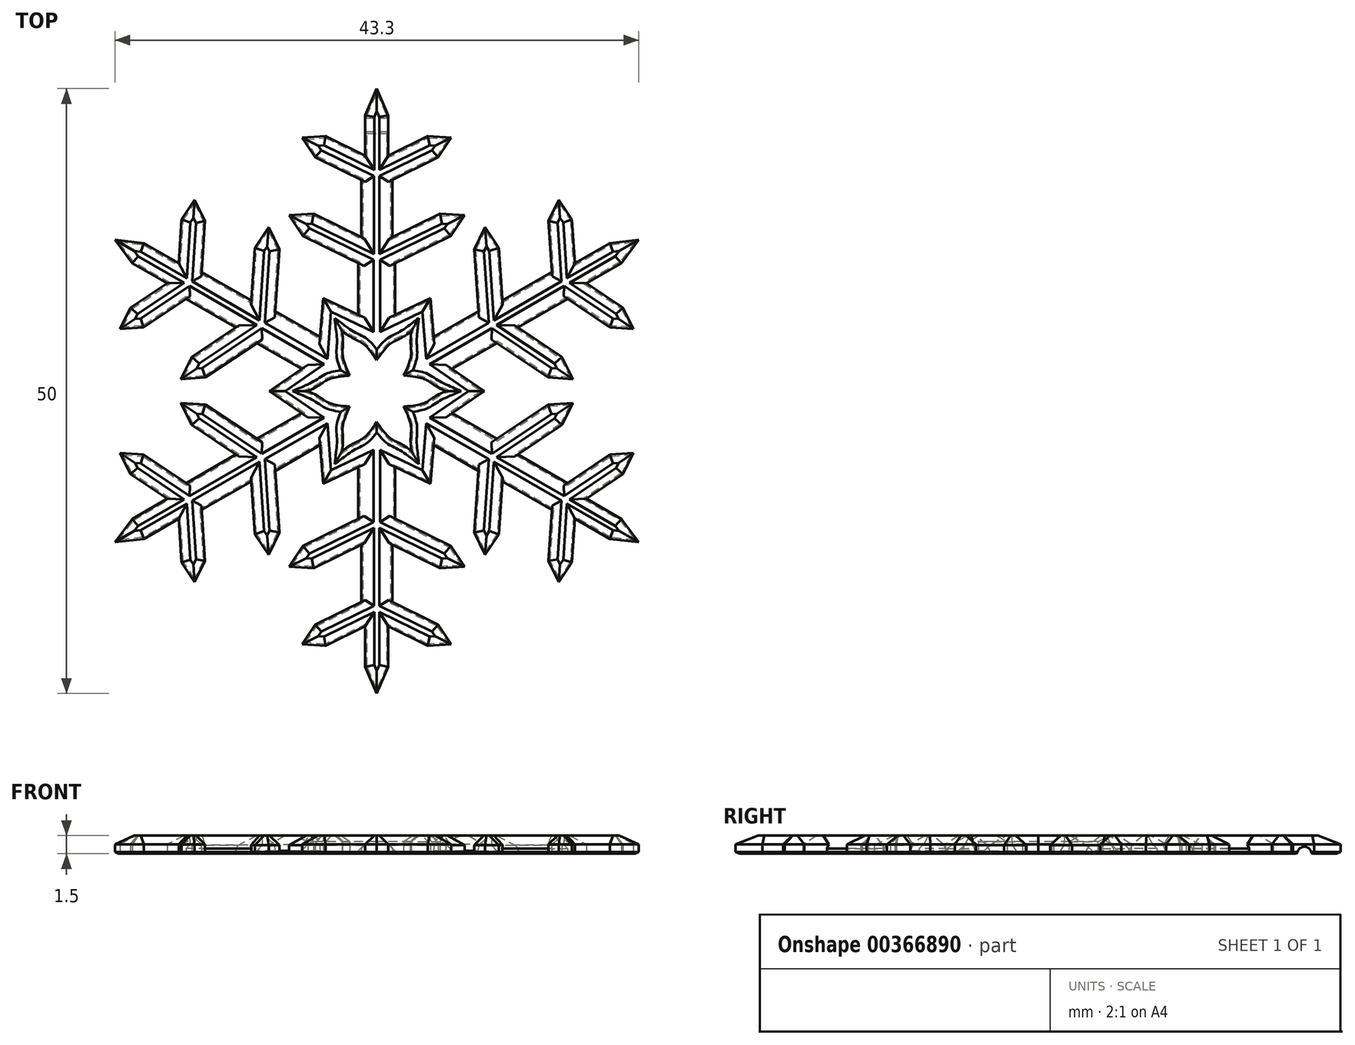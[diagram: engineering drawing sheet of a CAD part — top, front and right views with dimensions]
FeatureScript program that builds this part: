
annotation { "Feature Type Name" : "Feature", "Feature Type Description" : "" }
export const myFeature = defineFeature(function(context is Context, id is Id, definition is map)
    precondition{}
    {
        {
            var Q0;
            Q0=qCreatedBy(makeId("Top.planeOp"),FACE);
            var sketch = newSketch(context, id + "F0", { "sketchPlane" : qUnion([Q0])});
            skLineSegment(sketch, "E0", {"start": v(0, 0) * mm, "end": v(0, 29.9) * mm, "construction": true});
            skCircle(sketch, "E1", {"center": v(0, 0) * mm, "radius": 25 * mm, "construction": true});
            skLineSegment(sketch, "E2", {"start": v(0, 25) * mm, "end": v(0.95, 22.8) * mm});
            skLineSegment(sketch, "E3", {"start": v(0.95, 22.8) * mm, "end": v(0.95, 19.45) * mm});
            skLineSegment(sketch, "E4", {"start": v(0.95, 19.45) * mm, "end": v(4.22, 21.06) * mm});
            skLineSegment(sketch, "E5", {"start": v(4.22, 21.06) * mm, "end": v(6.16, 20.93) * mm});
            skLineSegment(sketch, "E6", {"start": v(6.16, 20.93) * mm, "end": v(5.08, 19.32) * mm});
            skLineSegment(sketch, "E7", {"start": v(5.08, 19.32) * mm, "end": v(1.28, 17.45) * mm});
            skLineSegment(sketch, "E8", {"start": v(1.28, 17.45) * mm, "end": v(1.28, 12.72) * mm});
            skLineSegment(sketch, "E9", {"start": v(1.28, 12.72) * mm, "end": v(5.21, 14.66) * mm});
            skLineSegment(sketch, "E10", {"start": v(5.21, 14.66) * mm, "end": v(7.25, 14.52) * mm});
            skLineSegment(sketch, "E11", {"start": v(7.25, 14.52) * mm, "end": v(6.11, 12.82) * mm});
            skLineSegment(sketch, "E12", {"start": v(6.11, 12.82) * mm, "end": v(1.52, 10.57) * mm});
            skLineSegment(sketch, "E13", {"start": v(1.52, 10.57) * mm, "end": v(1.52, 6.3) * mm});
            skLineSegment(sketch, "E14", {"start": v(1.52, 6.3) * mm, "end": v(4.43, 7.68) * mm});
            skLineSegment(sketch, "E15.MirrorCS", {"start": v(-0.95, 22.8) * mm, "end": v(-0.95, 19.45) * mm});
            skLineSegment(sketch, "E16.MirrorCS", {"start": v(-4.22, 21.06) * mm, "end": v(-6.16, 20.93) * mm});
            skLineSegment(sketch, "E17.MirrorCS", {"start": v(-0.95, 19.45) * mm, "end": v(-4.22, 21.06) * mm});
            skLineSegment(sketch, "E18.MirrorCS", {"start": v(-1.28, 12.72) * mm, "end": v(-5.21, 14.66) * mm});
            skLineSegment(sketch, "E19.MirrorCS", {"start": v(-5.21, 14.66) * mm, "end": v(-7.25, 14.52) * mm});
            skLineSegment(sketch, "E20.MirrorCS", {"start": v(-7.25, 14.52) * mm, "end": v(-6.11, 12.82) * mm});
            skLineSegment(sketch, "E21.MirrorCS", {"start": v(-1.28, 17.45) * mm, "end": v(-1.28, 12.72) * mm});
            skLineSegment(sketch, "E22.MirrorCS", {"start": v(0, 25) * mm, "end": v(-0.95, 22.8) * mm});
            skLineSegment(sketch, "E23.MirrorCS", {"start": v(-6.16, 20.93) * mm, "end": v(-5.08, 19.32) * mm});
            skLineSegment(sketch, "E24.MirrorCS", {"start": v(-5.08, 19.32) * mm, "end": v(-1.28, 17.45) * mm});
            skLineSegment(sketch, "E25.MirrorCS", {"start": v(-6.11, 12.82) * mm, "end": v(-1.52, 10.57) * mm});
            skLineSegment(sketch, "E26", {"start": v(0, 0) * mm, "end": v(0, 30.32) * mm, "construction": true});
            skLineSegment(sketch, "E27", {"start": v(0, 0) * mm, "end": v(17.52, 30.35) * mm, "construction": true});
            skLineSegment(sketch, "E28", {"start": v(0, 0) * mm, "end": v(-18.63, 32.26) * mm, "construction": true});
            skLineSegment(sketch, "E29", {"start": v(4.43, 7.68) * mm, "end": v(2.85, 4.93) * mm});
            skLineSegment(sketch, "E30.MirrorCS", {"start": v(-1.52, 10.57) * mm, "end": v(-1.52, 6.3) * mm});
            skLineSegment(sketch, "E31.MirrorCS", {"start": v(-1.52, 6.3) * mm, "end": v(-4.43, 7.68) * mm});
            skFitSpline(sketch, "E32", {"points": [v(2.85, 4.93) * mm, v(0, 2.57) * mm], "startDerivative": vector(-4.57, -3.43) * mm, "endDerivative": vector(-3.94, -5.85) * mm});
            skFitSpline(sketch, "E33.MirrorCS", {"points": [v(-2.85, 4.93) * mm, v(0, 2.57) * mm], "startDerivative": vector(4.57, -3.43) * mm, "endDerivative": vector(3.94, -5.85) * mm});
            skLineSegment(sketch, "E34.MirrorCS", {"start": v(-4.43, 7.68) * mm, "end": v(-2.85, 4.93) * mm});
            skSolve(sketch);
        }
        {
            var Q0;
            Q0=makeQuery(id+"F0.imprint","IMPRINT",FACE,{"disambiguationData":[TD([[makeQuery(id+"F0.imprint","IMPRINT",EDGE,{"derivedFrom":sQuery(id+"F0.wireOp",EDGE,"E2")}),-1.0]])]});
            extrude(context, id + "F1", {"entities" : qUnion([Q0]), "endBound" : BoundingType.SYMMETRIC, "depth" : 1.5 * mm});
        }
        {
            var Q0;
            Q0=qCreatedBy(makeId("Front.planeOp"),FACE);
            var sketch = newSketch(context, id + "F2", { "sketchPlane" : qUnion([Q0])});
            skLineSegment(sketch, "E35", {"start": v(0, -15.67) * mm, "end": v(0, 28.6) * mm, "construction": true});
            skSolve(sketch);
        }
        {
            var Q0;
            Q0=makeQuery(id+"F1.opExtrude","SWEPT_BODY",BODY,{"disambiguationData":[OSD([sQuery(id+"F0.wireOp",EDGE,"E2"),sQuery(id+"F0.wireOp",EDGE,"E3"),sQuery(id+"F0.wireOp",EDGE,"E4"),sQuery(id+"F0.wireOp",EDGE,"E5"),sQuery(id+"F0.wireOp",EDGE,"E6"),sQuery(id+"F0.wireOp",EDGE,"E7"),sQuery(id+"F0.wireOp",EDGE,"E8"),sQuery(id+"F0.wireOp",EDGE,"E9"),sQuery(id+"F0.wireOp",EDGE,"E10"),sQuery(id+"F0.wireOp",EDGE,"E11"),sQuery(id+"F0.wireOp",EDGE,"E12"),sQuery(id+"F0.wireOp",EDGE,"E13"),sQuery(id+"F0.wireOp",EDGE,"E14"),sQuery(id+"F0.wireOp",EDGE,"b2b48e4d-2c92-4a1f-81ad-3469f6dd68cb"),sQuery(id+"F0.wireOp",EDGE,"E15.MirrorCS"),sQuery(id+"F0.wireOp",EDGE,"E16.MirrorCS"),sQuery(id+"F0.wireOp",EDGE,"E17.MirrorCS"),sQuery(id+"F0.wireOp",EDGE,"E18.MirrorCS"),sQuery(id+"F0.wireOp",EDGE,"E19.MirrorCS"),sQuery(id+"F0.wireOp",EDGE,"E20.MirrorCS"),sQuery(id+"F0.wireOp",EDGE,"E21.MirrorCS"),sQuery(id+"F0.wireOp",EDGE,"E22.MirrorCS"),sQuery(id+"F0.wireOp",EDGE,"E23.MirrorCS"),sQuery(id+"F0.wireOp",EDGE,"E24.MirrorCS"),sQuery(id+"F0.wireOp",EDGE,"E160.MirrorCS"),sQuery(id+"F0.wireOp",EDGE,"E25.MirrorCS"),sQuery(id+"F0.wireOp",EDGE,"4b62aa35-2862-45d5-86f5-f30a92808e40"),sQuery(id+"F0.wireOp",EDGE,"c1be86ca-d8b8-4c1e-b1f3-8d63ae980cd1")])]});
            var Q1;
            Q1=sQuery(id+"F2.wireOp",EDGE,"E35");
            circularPattern(context, id + "F3", {"operationType" : NewBodyOperationType.ADD, "entities" : qUnion([Q0]), "axis" : qUnion([Q1]), "angle" : 360 * degree, "instanceCount" : round(6), "equalSpace" : true});
        }
        {
            var Q0;
            Q0=qCreatedBy(makeId("Front.planeOp"),FACE);
            cPlane(context, id + "F4", {"entities" : qUnion([Q0]), "cplaneType" : CPlaneType.OFFSET, "offset" : 25 * mm, "oppositeDirection" : true, "width" : 150 * mm, "height" : 150 * mm});
        }
        {
            var Q0;
            Q0=makeQuery(id+"F3.opPattern","COPY",EDGE,{"derivedFrom":makeQuery(id+"F1.opExtrude","CAP_EDGE",EDGE,{"disambiguationData":[OSD([sQuery(id+"F0.wireOp",EDGE,"E24.MirrorCS")])],"isStart":false}),"instanceName":"2"});
            var Q1;
            Q1=makeQuery(id+"F3.opPattern","COPY",EDGE,{"derivedFrom":makeQuery(id+"F1.opExtrude","CAP_EDGE",EDGE,{"disambiguationData":[OSD([sQuery(id+"F0.wireOp",EDGE,"E23.MirrorCS")])],"isStart":false}),"instanceName":"2"});
            var Q2;
            Q2=makeQuery(id+"F3.opPattern","COPY",EDGE,{"derivedFrom":makeQuery(id+"F1.opExtrude","CAP_EDGE",EDGE,{"disambiguationData":[OSD([sQuery(id+"F0.wireOp",EDGE,"E16.MirrorCS")])],"isStart":false}),"instanceName":"2"});
            var Q3;
            Q3=makeQuery(id+"F3.opPattern","COPY",EDGE,{"derivedFrom":makeQuery(id+"F1.opExtrude","CAP_EDGE",EDGE,{"disambiguationData":[OSD([sQuery(id+"F0.wireOp",EDGE,"E17.MirrorCS")])],"isStart":false}),"instanceName":"2"});
            var Q4;
            Q4=makeQuery(id+"F3.opPattern","COPY",EDGE,{"derivedFrom":makeQuery(id+"F1.opExtrude","CAP_EDGE",EDGE,{"disambiguationData":[OSD([sQuery(id+"F0.wireOp",EDGE,"E15.MirrorCS")])],"isStart":false}),"instanceName":"2"});
            var Q5;
            Q5=makeQuery(id+"F3.opPattern","COPY",EDGE,{"derivedFrom":makeQuery(id+"F1.opExtrude","CAP_EDGE",EDGE,{"disambiguationData":[OSD([sQuery(id+"F0.wireOp",EDGE,"E22.MirrorCS")])],"isStart":false}),"instanceName":"2"});
            var Q6;
            Q6=makeQuery(id+"F3.opPattern","COPY",EDGE,{"derivedFrom":makeQuery(id+"F1.opExtrude","CAP_EDGE",EDGE,{"disambiguationData":[OSD([sQuery(id+"F0.wireOp",EDGE,"E2")])],"isStart":false}),"instanceName":"2"});
            var Q7;
            Q7=makeQuery(id+"F3.opPattern","COPY",EDGE,{"derivedFrom":makeQuery(id+"F1.opExtrude","CAP_EDGE",EDGE,{"disambiguationData":[OSD([sQuery(id+"F0.wireOp",EDGE,"E3")])],"isStart":false}),"instanceName":"2"});
            var Q8;
            Q8=makeQuery(id+"F3.opPattern","COPY",EDGE,{"derivedFrom":makeQuery(id+"F1.opExtrude","CAP_EDGE",EDGE,{"disambiguationData":[OSD([sQuery(id+"F0.wireOp",EDGE,"E4")])],"isStart":false}),"instanceName":"2"});
            var Q9;
            Q9=makeQuery(id+"F3.opPattern","COPY",EDGE,{"derivedFrom":makeQuery(id+"F1.opExtrude","CAP_EDGE",EDGE,{"disambiguationData":[OSD([sQuery(id+"F0.wireOp",EDGE,"E5")])],"isStart":false}),"instanceName":"2"});
            var Q10;
            Q10=makeQuery(id+"F3.opPattern","COPY",EDGE,{"derivedFrom":makeQuery(id+"F1.opExtrude","CAP_EDGE",EDGE,{"disambiguationData":[OSD([sQuery(id+"F0.wireOp",EDGE,"E6")])],"isStart":false}),"instanceName":"2"});
            var Q11;
            Q11=makeQuery(id+"F3.opPattern","COPY",EDGE,{"derivedFrom":makeQuery(id+"F1.opExtrude","CAP_EDGE",EDGE,{"disambiguationData":[OSD([sQuery(id+"F0.wireOp",EDGE,"E7")])],"isStart":false}),"instanceName":"2"});
            var Q12;
            Q12=makeQuery(id+"F3.opPattern","COPY",EDGE,{"derivedFrom":makeQuery(id+"F1.opExtrude","CAP_EDGE",EDGE,{"disambiguationData":[OSD([sQuery(id+"F0.wireOp",EDGE,"E14")])],"isStart":false}),"instanceName":"2"});
            var Q13;
            Q13=makeQuery(id+"F3.opPattern","COPY",EDGE,{"derivedFrom":makeQuery(id+"F1.opExtrude","CAP_EDGE",EDGE,{"disambiguationData":[OSD([sQuery(id+"F0.wireOp",EDGE,"E31.MirrorCS")])],"isStart":false}),"instanceName":"2"});
            var Q14;
            Q14=makeQuery(id+"F3.opPattern","COPY",EDGE,{"derivedFrom":makeQuery(id+"F1.opExtrude","CAP_EDGE",EDGE,{"disambiguationData":[OSD([sQuery(id+"F0.wireOp",EDGE,"E24.MirrorCS")])],"isStart":false}),"instanceName":"1"});
            var Q15;
            Q15=makeQuery(id+"F3.opPattern","COPY",EDGE,{"derivedFrom":makeQuery(id+"F1.opExtrude","CAP_EDGE",EDGE,{"disambiguationData":[OSD([sQuery(id+"F0.wireOp",EDGE,"E23.MirrorCS")])],"isStart":false}),"instanceName":"1"});
            var Q16;
            Q16=makeQuery(id+"F3.opPattern","COPY",EDGE,{"derivedFrom":makeQuery(id+"F1.opExtrude","CAP_EDGE",EDGE,{"disambiguationData":[OSD([sQuery(id+"F0.wireOp",EDGE,"E16.MirrorCS")])],"isStart":false}),"instanceName":"1"});
            var Q17;
            Q17=makeQuery(id+"F3.opPattern","COPY",EDGE,{"derivedFrom":makeQuery(id+"F1.opExtrude","CAP_EDGE",EDGE,{"disambiguationData":[OSD([sQuery(id+"F0.wireOp",EDGE,"E17.MirrorCS")])],"isStart":false}),"instanceName":"1"});
            var Q18;
            Q18=makeQuery(id+"F3.opPattern","COPY",EDGE,{"derivedFrom":makeQuery(id+"F1.opExtrude","CAP_EDGE",EDGE,{"disambiguationData":[OSD([sQuery(id+"F0.wireOp",EDGE,"E15.MirrorCS")])],"isStart":false}),"instanceName":"1"});
            var Q19;
            Q19=makeQuery(id+"F3.opPattern","COPY",EDGE,{"derivedFrom":makeQuery(id+"F1.opExtrude","CAP_EDGE",EDGE,{"disambiguationData":[OSD([sQuery(id+"F0.wireOp",EDGE,"E22.MirrorCS")])],"isStart":false}),"instanceName":"1"});
            var Q20;
            Q20=makeQuery(id+"F3.opPattern","COPY",EDGE,{"derivedFrom":makeQuery(id+"F1.opExtrude","CAP_EDGE",EDGE,{"disambiguationData":[OSD([sQuery(id+"F0.wireOp",EDGE,"E2")])],"isStart":false}),"instanceName":"1"});
            var Q21;
            Q21=makeQuery(id+"F3.opPattern","COPY",EDGE,{"derivedFrom":makeQuery(id+"F1.opExtrude","CAP_EDGE",EDGE,{"disambiguationData":[OSD([sQuery(id+"F0.wireOp",EDGE,"E3")])],"isStart":false}),"instanceName":"1"});
            var Q22;
            Q22=makeQuery(id+"F3.opPattern","COPY",EDGE,{"derivedFrom":makeQuery(id+"F1.opExtrude","CAP_EDGE",EDGE,{"disambiguationData":[OSD([sQuery(id+"F0.wireOp",EDGE,"E4")])],"isStart":false}),"instanceName":"1"});
            var Q23;
            Q23=makeQuery(id+"F3.opPattern","COPY",EDGE,{"derivedFrom":makeQuery(id+"F1.opExtrude","CAP_EDGE",EDGE,{"disambiguationData":[OSD([sQuery(id+"F0.wireOp",EDGE,"E5")])],"isStart":false}),"instanceName":"1"});
            var Q24;
            Q24=makeQuery(id+"F3.opPattern","COPY",EDGE,{"derivedFrom":makeQuery(id+"F1.opExtrude","CAP_EDGE",EDGE,{"disambiguationData":[OSD([sQuery(id+"F0.wireOp",EDGE,"E6")])],"isStart":false}),"instanceName":"1"});
            var Q25;
            Q25=makeQuery(id+"F3.opPattern","COPY",EDGE,{"derivedFrom":makeQuery(id+"F1.opExtrude","CAP_EDGE",EDGE,{"disambiguationData":[OSD([sQuery(id+"F0.wireOp",EDGE,"E7")])],"isStart":false}),"instanceName":"1"});
            var Q26;
            Q26=makeQuery(id+"F3.opPattern","COPY",EDGE,{"derivedFrom":makeQuery(id+"F1.opExtrude","CAP_EDGE",EDGE,{"disambiguationData":[OSD([sQuery(id+"F0.wireOp",EDGE,"E31.MirrorCS")])],"isStart":false}),"instanceName":"1"});
            var Q27;
            Q27=makeQuery(id+"F3.opPattern","COPY",EDGE,{"derivedFrom":makeQuery(id+"F1.opExtrude","CAP_EDGE",EDGE,{"disambiguationData":[OSD([sQuery(id+"F0.wireOp",EDGE,"E14")])],"isStart":false}),"instanceName":"1"});
            var Q28;
            Q28=makeQuery(id+"F1.opExtrude","CAP_EDGE",EDGE,{"disambiguationData":[OSD([sQuery(id+"F0.wireOp",EDGE,"E23.MirrorCS")])],"isStart":false});
            var Q29;
            Q29=makeQuery(id+"F1.opExtrude","CAP_EDGE",EDGE,{"disambiguationData":[OSD([sQuery(id+"F0.wireOp",EDGE,"E16.MirrorCS")])],"isStart":false});
            var Q30;
            Q30=makeQuery(id+"F1.opExtrude","CAP_EDGE",EDGE,{"disambiguationData":[OSD([sQuery(id+"F0.wireOp",EDGE,"E17.MirrorCS")])],"isStart":false});
            var Q31;
            Q31=makeQuery(id+"F1.opExtrude","CAP_EDGE",EDGE,{"disambiguationData":[OSD([sQuery(id+"F0.wireOp",EDGE,"E15.MirrorCS")])],"isStart":false});
            var Q32;
            Q32=makeQuery(id+"F1.opExtrude","CAP_EDGE",EDGE,{"disambiguationData":[OSD([sQuery(id+"F0.wireOp",EDGE,"E22.MirrorCS")])],"isStart":false});
            var Q33;
            Q33=makeQuery(id+"F1.opExtrude","CAP_EDGE",EDGE,{"disambiguationData":[OSD([sQuery(id+"F0.wireOp",EDGE,"E2")])],"isStart":false});
            var Q34;
            Q34=makeQuery(id+"F1.opExtrude","CAP_EDGE",EDGE,{"disambiguationData":[OSD([sQuery(id+"F0.wireOp",EDGE,"E3")])],"isStart":false});
            var Q35;
            Q35=makeQuery(id+"F1.opExtrude","CAP_EDGE",EDGE,{"disambiguationData":[OSD([sQuery(id+"F0.wireOp",EDGE,"E4")])],"isStart":false});
            var Q36;
            Q36=makeQuery(id+"F1.opExtrude","CAP_EDGE",EDGE,{"disambiguationData":[OSD([sQuery(id+"F0.wireOp",EDGE,"E5")])],"isStart":false});
            var Q37;
            Q37=makeQuery(id+"F1.opExtrude","CAP_EDGE",EDGE,{"disambiguationData":[OSD([sQuery(id+"F0.wireOp",EDGE,"E6")])],"isStart":false});
            var Q38;
            Q38=makeQuery(id+"F1.opExtrude","CAP_EDGE",EDGE,{"disambiguationData":[OSD([sQuery(id+"F0.wireOp",EDGE,"E7")])],"isStart":false});
            var Q39;
            Q39=makeQuery(id+"F1.opExtrude","CAP_EDGE",EDGE,{"disambiguationData":[OSD([sQuery(id+"F0.wireOp",EDGE,"E31.MirrorCS")])],"isStart":false});
            var Q40;
            Q40=makeQuery(id+"F1.opExtrude","CAP_EDGE",EDGE,{"disambiguationData":[OSD([sQuery(id+"F0.wireOp",EDGE,"E14")])],"isStart":false});
            var Q41;
            Q41=makeQuery(id+"F3.opPattern","COPY",EDGE,{"derivedFrom":makeQuery(id+"F1.opExtrude","CAP_EDGE",EDGE,{"disambiguationData":[OSD([sQuery(id+"F0.wireOp",EDGE,"E24.MirrorCS")])],"isStart":false}),"instanceName":"5"});
            var Q42;
            Q42=makeQuery(id+"F3.opPattern","COPY",EDGE,{"derivedFrom":makeQuery(id+"F1.opExtrude","CAP_EDGE",EDGE,{"disambiguationData":[OSD([sQuery(id+"F0.wireOp",EDGE,"E23.MirrorCS")])],"isStart":false}),"instanceName":"5"});
            var Q43;
            Q43=makeQuery(id+"F3.opPattern","COPY",EDGE,{"derivedFrom":makeQuery(id+"F1.opExtrude","CAP_EDGE",EDGE,{"disambiguationData":[OSD([sQuery(id+"F0.wireOp",EDGE,"E16.MirrorCS")])],"isStart":false}),"instanceName":"5"});
            var Q44;
            Q44=makeQuery(id+"F3.opPattern","COPY",EDGE,{"derivedFrom":makeQuery(id+"F1.opExtrude","CAP_EDGE",EDGE,{"disambiguationData":[OSD([sQuery(id+"F0.wireOp",EDGE,"E15.MirrorCS")])],"isStart":false}),"instanceName":"5"});
            var Q45;
            Q45=makeQuery(id+"F3.opPattern","COPY",EDGE,{"derivedFrom":makeQuery(id+"F1.opExtrude","CAP_EDGE",EDGE,{"disambiguationData":[OSD([sQuery(id+"F0.wireOp",EDGE,"E17.MirrorCS")])],"isStart":false}),"instanceName":"5"});
            var Q46;
            Q46=makeQuery(id+"F3.opPattern","COPY",EDGE,{"derivedFrom":makeQuery(id+"F1.opExtrude","CAP_EDGE",EDGE,{"disambiguationData":[OSD([sQuery(id+"F0.wireOp",EDGE,"E22.MirrorCS")])],"isStart":false}),"instanceName":"5"});
            var Q47;
            Q47=makeQuery(id+"F3.opPattern","COPY",EDGE,{"derivedFrom":makeQuery(id+"F1.opExtrude","CAP_EDGE",EDGE,{"disambiguationData":[OSD([sQuery(id+"F0.wireOp",EDGE,"E2")])],"isStart":false}),"instanceName":"5"});
            var Q48;
            Q48=makeQuery(id+"F3.opPattern","COPY",EDGE,{"derivedFrom":makeQuery(id+"F1.opExtrude","CAP_EDGE",EDGE,{"disambiguationData":[OSD([sQuery(id+"F0.wireOp",EDGE,"E3")])],"isStart":false}),"instanceName":"5"});
            var Q49;
            Q49=makeQuery(id+"F3.opPattern","COPY",EDGE,{"derivedFrom":makeQuery(id+"F1.opExtrude","CAP_EDGE",EDGE,{"disambiguationData":[OSD([sQuery(id+"F0.wireOp",EDGE,"E4")])],"isStart":false}),"instanceName":"5"});
            var Q50;
            Q50=makeQuery(id+"F3.opPattern","COPY",EDGE,{"derivedFrom":makeQuery(id+"F1.opExtrude","CAP_EDGE",EDGE,{"disambiguationData":[OSD([sQuery(id+"F0.wireOp",EDGE,"E5")])],"isStart":false}),"instanceName":"5"});
            var Q51;
            Q51=makeQuery(id+"F3.opPattern","COPY",EDGE,{"derivedFrom":makeQuery(id+"F1.opExtrude","CAP_EDGE",EDGE,{"disambiguationData":[OSD([sQuery(id+"F0.wireOp",EDGE,"E6")])],"isStart":false}),"instanceName":"5"});
            var Q52;
            Q52=makeQuery(id+"F3.opPattern","COPY",EDGE,{"derivedFrom":makeQuery(id+"F1.opExtrude","CAP_EDGE",EDGE,{"disambiguationData":[OSD([sQuery(id+"F0.wireOp",EDGE,"E7")])],"isStart":false}),"instanceName":"5"});
            var Q53;
            Q53=makeQuery(id+"F3.opPattern","COPY",EDGE,{"derivedFrom":makeQuery(id+"F1.opExtrude","CAP_EDGE",EDGE,{"disambiguationData":[OSD([sQuery(id+"F0.wireOp",EDGE,"E31.MirrorCS")])],"isStart":false}),"instanceName":"5"});
            var Q54;
            Q54=makeQuery(id+"F3.opPattern","COPY",EDGE,{"derivedFrom":makeQuery(id+"F1.opExtrude","CAP_EDGE",EDGE,{"disambiguationData":[OSD([sQuery(id+"F0.wireOp",EDGE,"E14")])],"isStart":false}),"instanceName":"5"});
            var Q55;
            Q55=makeQuery(id+"F3.opPattern","COPY",EDGE,{"derivedFrom":makeQuery(id+"F1.opExtrude","CAP_EDGE",EDGE,{"disambiguationData":[OSD([sQuery(id+"F0.wireOp",EDGE,"E24.MirrorCS")])],"isStart":false}),"instanceName":"4"});
            var Q56;
            Q56=makeQuery(id+"F3.opPattern","COPY",EDGE,{"derivedFrom":makeQuery(id+"F1.opExtrude","CAP_EDGE",EDGE,{"disambiguationData":[OSD([sQuery(id+"F0.wireOp",EDGE,"E23.MirrorCS")])],"isStart":false}),"instanceName":"4"});
            var Q57;
            Q57=makeQuery(id+"F3.opPattern","COPY",EDGE,{"derivedFrom":makeQuery(id+"F1.opExtrude","CAP_EDGE",EDGE,{"disambiguationData":[OSD([sQuery(id+"F0.wireOp",EDGE,"E16.MirrorCS")])],"isStart":false}),"instanceName":"4"});
            var Q58;
            Q58=makeQuery(id+"F3.opPattern","COPY",EDGE,{"derivedFrom":makeQuery(id+"F1.opExtrude","CAP_EDGE",EDGE,{"disambiguationData":[OSD([sQuery(id+"F0.wireOp",EDGE,"E17.MirrorCS")])],"isStart":false}),"instanceName":"4"});
            var Q59;
            Q59=makeQuery(id+"F3.opPattern","COPY",EDGE,{"derivedFrom":makeQuery(id+"F1.opExtrude","CAP_EDGE",EDGE,{"disambiguationData":[OSD([sQuery(id+"F0.wireOp",EDGE,"E15.MirrorCS")])],"isStart":false}),"instanceName":"4"});
            var Q60;
            Q60=makeQuery(id+"F3.opPattern","COPY",EDGE,{"derivedFrom":makeQuery(id+"F1.opExtrude","CAP_EDGE",EDGE,{"disambiguationData":[OSD([sQuery(id+"F0.wireOp",EDGE,"E22.MirrorCS")])],"isStart":false}),"instanceName":"4"});
            var Q61;
            Q61=makeQuery(id+"F3.opPattern","COPY",EDGE,{"derivedFrom":makeQuery(id+"F1.opExtrude","CAP_EDGE",EDGE,{"disambiguationData":[OSD([sQuery(id+"F0.wireOp",EDGE,"E2")])],"isStart":false}),"instanceName":"4"});
            var Q62;
            Q62=makeQuery(id+"F3.opPattern","COPY",EDGE,{"derivedFrom":makeQuery(id+"F1.opExtrude","CAP_EDGE",EDGE,{"disambiguationData":[OSD([sQuery(id+"F0.wireOp",EDGE,"E3")])],"isStart":false}),"instanceName":"4"});
            var Q63;
            Q63=makeQuery(id+"F3.opPattern","COPY",EDGE,{"derivedFrom":makeQuery(id+"F1.opExtrude","CAP_EDGE",EDGE,{"disambiguationData":[OSD([sQuery(id+"F0.wireOp",EDGE,"E4")])],"isStart":false}),"instanceName":"4"});
            var Q64;
            Q64=makeQuery(id+"F3.opPattern","COPY",EDGE,{"derivedFrom":makeQuery(id+"F1.opExtrude","CAP_EDGE",EDGE,{"disambiguationData":[OSD([sQuery(id+"F0.wireOp",EDGE,"E5")])],"isStart":false}),"instanceName":"4"});
            var Q65;
            Q65=makeQuery(id+"F3.opPattern","COPY",EDGE,{"derivedFrom":makeQuery(id+"F1.opExtrude","CAP_EDGE",EDGE,{"disambiguationData":[OSD([sQuery(id+"F0.wireOp",EDGE,"E6")])],"isStart":false}),"instanceName":"4"});
            var Q66;
            Q66=makeQuery(id+"F3.opPattern","COPY",EDGE,{"derivedFrom":makeQuery(id+"F1.opExtrude","CAP_EDGE",EDGE,{"disambiguationData":[OSD([sQuery(id+"F0.wireOp",EDGE,"E7")])],"isStart":false}),"instanceName":"4"});
            var Q67;
            Q67=makeQuery(id+"F3.opPattern","COPY",EDGE,{"derivedFrom":makeQuery(id+"F1.opExtrude","CAP_EDGE",EDGE,{"disambiguationData":[OSD([sQuery(id+"F0.wireOp",EDGE,"E31.MirrorCS")])],"isStart":false}),"instanceName":"4"});
            var Q68;
            Q68=makeQuery(id+"F3.opPattern","COPY",EDGE,{"derivedFrom":makeQuery(id+"F1.opExtrude","CAP_EDGE",EDGE,{"disambiguationData":[OSD([sQuery(id+"F0.wireOp",EDGE,"E14")])],"isStart":false}),"instanceName":"4"});
            var Q69;
            Q69=makeQuery(id+"F3.opPattern","COPY",EDGE,{"derivedFrom":makeQuery(id+"F1.opExtrude","CAP_EDGE",EDGE,{"disambiguationData":[OSD([sQuery(id+"F0.wireOp",EDGE,"E24.MirrorCS")])],"isStart":false}),"instanceName":"3"});
            var Q70;
            Q70=makeQuery(id+"F3.opPattern","COPY",EDGE,{"derivedFrom":makeQuery(id+"F1.opExtrude","CAP_EDGE",EDGE,{"disambiguationData":[OSD([sQuery(id+"F0.wireOp",EDGE,"E23.MirrorCS")])],"isStart":false}),"instanceName":"3"});
            var Q71;
            Q71=makeQuery(id+"F3.opPattern","COPY",EDGE,{"derivedFrom":makeQuery(id+"F1.opExtrude","CAP_EDGE",EDGE,{"disambiguationData":[OSD([sQuery(id+"F0.wireOp",EDGE,"E16.MirrorCS")])],"isStart":false}),"instanceName":"3"});
            var Q72;
            Q72=makeQuery(id+"F3.opPattern","COPY",EDGE,{"derivedFrom":makeQuery(id+"F1.opExtrude","CAP_EDGE",EDGE,{"disambiguationData":[OSD([sQuery(id+"F0.wireOp",EDGE,"E17.MirrorCS")])],"isStart":false}),"instanceName":"3"});
            var Q73;
            Q73=makeQuery(id+"F3.opPattern","COPY",EDGE,{"derivedFrom":makeQuery(id+"F1.opExtrude","CAP_EDGE",EDGE,{"disambiguationData":[OSD([sQuery(id+"F0.wireOp",EDGE,"E15.MirrorCS")])],"isStart":false}),"instanceName":"3"});
            var Q74;
            Q74=makeQuery(id+"F3.opPattern","COPY",EDGE,{"derivedFrom":makeQuery(id+"F1.opExtrude","CAP_EDGE",EDGE,{"disambiguationData":[OSD([sQuery(id+"F0.wireOp",EDGE,"E22.MirrorCS")])],"isStart":false}),"instanceName":"3"});
            var Q75;
            Q75=makeQuery(id+"F3.opPattern","COPY",EDGE,{"derivedFrom":makeQuery(id+"F1.opExtrude","CAP_EDGE",EDGE,{"disambiguationData":[OSD([sQuery(id+"F0.wireOp",EDGE,"E2")])],"isStart":false}),"instanceName":"3"});
            var Q76;
            Q76=makeQuery(id+"F3.opPattern","COPY",EDGE,{"derivedFrom":makeQuery(id+"F1.opExtrude","CAP_EDGE",EDGE,{"disambiguationData":[OSD([sQuery(id+"F0.wireOp",EDGE,"E3")])],"isStart":false}),"instanceName":"3"});
            var Q77;
            Q77=makeQuery(id+"F3.opPattern","COPY",EDGE,{"derivedFrom":makeQuery(id+"F1.opExtrude","CAP_EDGE",EDGE,{"disambiguationData":[OSD([sQuery(id+"F0.wireOp",EDGE,"E4")])],"isStart":false}),"instanceName":"3"});
            var Q78;
            Q78=makeQuery(id+"F3.opPattern","COPY",EDGE,{"derivedFrom":makeQuery(id+"F1.opExtrude","CAP_EDGE",EDGE,{"disambiguationData":[OSD([sQuery(id+"F0.wireOp",EDGE,"E5")])],"isStart":false}),"instanceName":"3"});
            var Q79;
            Q79=makeQuery(id+"F3.opPattern","COPY",EDGE,{"derivedFrom":makeQuery(id+"F1.opExtrude","CAP_EDGE",EDGE,{"disambiguationData":[OSD([sQuery(id+"F0.wireOp",EDGE,"E6")])],"isStart":false}),"instanceName":"3"});
            var Q80;
            Q80=makeQuery(id+"F3.opPattern","COPY",EDGE,{"derivedFrom":makeQuery(id+"F1.opExtrude","CAP_EDGE",EDGE,{"disambiguationData":[OSD([sQuery(id+"F0.wireOp",EDGE,"E7")])],"isStart":false}),"instanceName":"3"});
            var Q81;
            Q81=makeQuery(id+"F3.opPattern","COPY",EDGE,{"derivedFrom":makeQuery(id+"F1.opExtrude","CAP_EDGE",EDGE,{"disambiguationData":[OSD([sQuery(id+"F0.wireOp",EDGE,"E31.MirrorCS")])],"isStart":false}),"instanceName":"3"});
            var Q82;
            Q82=makeQuery(id+"F3.opPattern","COPY",EDGE,{"derivedFrom":makeQuery(id+"F1.opExtrude","CAP_EDGE",EDGE,{"disambiguationData":[OSD([sQuery(id+"F0.wireOp",EDGE,"E14")])],"isStart":false}),"instanceName":"3"});
            var Q83;
            Q83=makeQuery(id+"F1.opExtrude","CAP_EDGE",EDGE,{"disambiguationData":[OSD([sQuery(id+"F0.wireOp",EDGE,"E24.MirrorCS")])],"isStart":false});
            chamfer(context, id + "F5", {"entities" : qUnion([Q0, Q1, Q2, Q3, Q4, Q5, Q6, Q7, Q8, Q9, Q10, Q11, Q12, Q13, Q14, Q15, Q16, Q17, Q18, Q19, Q20, Q21, Q22, Q23, Q24, Q25, Q26, Q27, Q28, Q29, Q30, Q31, Q32, Q33, Q34, Q35, Q36, Q37, Q38, Q39, Q40, Q41, Q42, Q43, Q44, Q45, Q46, Q47, Q48, Q49, Q50, Q51, Q52, Q53, Q54, Q55, Q56, Q57, Q58, Q59, Q60, Q61, Q62, Q63, Q64, Q65, Q66, Q67, Q68, Q69, Q70, Q71, Q72, Q73, Q74, Q75, Q76, Q77, Q78, Q79, Q80, Q81, Q82, Q83]), "width" : .74 * mm, "tangentPropagation" : true});
        }
        {
            var Q0;
            Q0=makeQuery(id+"F3.opPattern","COPY",EDGE,{"derivedFrom":makeQuery(id+"F1.opExtrude","CAP_EDGE",EDGE,{"disambiguationData":[OSD([sQuery(id+"F0.wireOp",EDGE,"E21.MirrorCS")])],"isStart":false}),"instanceName":"2"});
            var Q1;
            Q1=makeQuery(id+"F3.opPattern","COPY",EDGE,{"derivedFrom":makeQuery(id+"F1.opExtrude","CAP_EDGE",EDGE,{"disambiguationData":[OSD([sQuery(id+"F0.wireOp",EDGE,"E8")])],"isStart":false}),"instanceName":"2"});
            var Q2;
            Q2=makeQuery(id+"F3.opPattern","COPY",EDGE,{"derivedFrom":makeQuery(id+"F1.opExtrude","CAP_EDGE",EDGE,{"disambiguationData":[OSD([sQuery(id+"F0.wireOp",EDGE,"E21.MirrorCS")])],"isStart":false}),"instanceName":"1"});
            var Q3;
            Q3=makeQuery(id+"F3.opPattern","COPY",EDGE,{"derivedFrom":makeQuery(id+"F1.opExtrude","CAP_EDGE",EDGE,{"disambiguationData":[OSD([sQuery(id+"F0.wireOp",EDGE,"E8")])],"isStart":false}),"instanceName":"1"});
            var Q4;
            Q4=makeQuery(id+"F1.opExtrude","CAP_EDGE",EDGE,{"disambiguationData":[OSD([sQuery(id+"F0.wireOp",EDGE,"E21.MirrorCS")])],"isStart":false});
            var Q5;
            Q5=makeQuery(id+"F1.opExtrude","CAP_EDGE",EDGE,{"disambiguationData":[OSD([sQuery(id+"F0.wireOp",EDGE,"E8")])],"isStart":false});
            var Q6;
            Q6=makeQuery(id+"F3.opPattern","COPY",EDGE,{"derivedFrom":makeQuery(id+"F1.opExtrude","CAP_EDGE",EDGE,{"disambiguationData":[OSD([sQuery(id+"F0.wireOp",EDGE,"E21.MirrorCS")])],"isStart":false}),"instanceName":"5"});
            var Q7;
            Q7=makeQuery(id+"F3.opPattern","COPY",EDGE,{"derivedFrom":makeQuery(id+"F1.opExtrude","CAP_EDGE",EDGE,{"disambiguationData":[OSD([sQuery(id+"F0.wireOp",EDGE,"E8")])],"isStart":false}),"instanceName":"5"});
            var Q8;
            Q8=makeQuery(id+"F3.opPattern","COPY",EDGE,{"derivedFrom":makeQuery(id+"F1.opExtrude","CAP_EDGE",EDGE,{"disambiguationData":[OSD([sQuery(id+"F0.wireOp",EDGE,"E21.MirrorCS")])],"isStart":false}),"instanceName":"4"});
            var Q9;
            Q9=makeQuery(id+"F3.opPattern","COPY",EDGE,{"derivedFrom":makeQuery(id+"F1.opExtrude","CAP_EDGE",EDGE,{"disambiguationData":[OSD([sQuery(id+"F0.wireOp",EDGE,"E8")])],"isStart":false}),"instanceName":"4"});
            var Q10;
            Q10=makeQuery(id+"F3.opPattern","COPY",EDGE,{"derivedFrom":makeQuery(id+"F1.opExtrude","CAP_EDGE",EDGE,{"disambiguationData":[OSD([sQuery(id+"F0.wireOp",EDGE,"E21.MirrorCS")])],"isStart":false}),"instanceName":"3"});
            var Q11;
            Q11=makeQuery(id+"F3.opPattern","COPY",EDGE,{"derivedFrom":makeQuery(id+"F1.opExtrude","CAP_EDGE",EDGE,{"disambiguationData":[OSD([sQuery(id+"F0.wireOp",EDGE,"E8")])],"isStart":false}),"instanceName":"3"});
            chamfer(context, id + "F6", {"entities" : qUnion([Q0, Q1, Q2, Q3, Q4, Q5, Q6, Q7, Q8, Q9, Q10, Q11]), "width" : 1.06 * mm, "tangentPropagation" : true});
        }
        {
            var Q0;
            Q0=makeQuery(id+"F3.opPattern","COPY",EDGE,{"derivedFrom":makeQuery(id+"F1.opExtrude","CAP_EDGE",EDGE,{"disambiguationData":[OSD([sQuery(id+"F0.wireOp",EDGE,"E18.MirrorCS")])],"isStart":false}),"instanceName":"2"});
            var Q1;
            Q1=makeQuery(id+"F3.opPattern","COPY",EDGE,{"derivedFrom":makeQuery(id+"F1.opExtrude","CAP_EDGE",EDGE,{"disambiguationData":[OSD([sQuery(id+"F0.wireOp",EDGE,"E19.MirrorCS")])],"isStart":false}),"instanceName":"2"});
            var Q2;
            Q2=makeQuery(id+"F3.opPattern","COPY",EDGE,{"derivedFrom":makeQuery(id+"F1.opExtrude","CAP_EDGE",EDGE,{"disambiguationData":[OSD([sQuery(id+"F0.wireOp",EDGE,"E20.MirrorCS")])],"isStart":false}),"instanceName":"2"});
            var Q3;
            Q3=makeQuery(id+"F3.opPattern","COPY",EDGE,{"derivedFrom":makeQuery(id+"F1.opExtrude","CAP_EDGE",EDGE,{"disambiguationData":[OSD([sQuery(id+"F0.wireOp",EDGE,"E25.MirrorCS")])],"isStart":false}),"instanceName":"2"});
            var Q4;
            Q4=makeQuery(id+"F3.opPattern","COPY",EDGE,{"derivedFrom":makeQuery(id+"F1.opExtrude","CAP_EDGE",EDGE,{"disambiguationData":[OSD([sQuery(id+"F0.wireOp",EDGE,"E9")])],"isStart":false}),"instanceName":"2"});
            var Q5;
            Q5=makeQuery(id+"F3.opPattern","COPY",EDGE,{"derivedFrom":makeQuery(id+"F1.opExtrude","CAP_EDGE",EDGE,{"disambiguationData":[OSD([sQuery(id+"F0.wireOp",EDGE,"E10")])],"isStart":false}),"instanceName":"2"});
            var Q6;
            Q6=makeQuery(id+"F3.opPattern","COPY",EDGE,{"derivedFrom":makeQuery(id+"F1.opExtrude","CAP_EDGE",EDGE,{"disambiguationData":[OSD([sQuery(id+"F0.wireOp",EDGE,"E11")])],"isStart":false}),"instanceName":"2"});
            var Q7;
            Q7=makeQuery(id+"F3.opPattern","COPY",EDGE,{"derivedFrom":makeQuery(id+"F1.opExtrude","CAP_EDGE",EDGE,{"disambiguationData":[OSD([sQuery(id+"F0.wireOp",EDGE,"E12")])],"isStart":false}),"instanceName":"2"});
            var Q8;
            Q8=makeQuery(id+"F3.opPattern","COPY",EDGE,{"derivedFrom":makeQuery(id+"F1.opExtrude","CAP_EDGE",EDGE,{"disambiguationData":[OSD([sQuery(id+"F0.wireOp",EDGE,"E20.MirrorCS")])],"isStart":false}),"instanceName":"1"});
            var Q9;
            Q9=makeQuery(id+"F3.opPattern","COPY",EDGE,{"derivedFrom":makeQuery(id+"F1.opExtrude","CAP_EDGE",EDGE,{"disambiguationData":[OSD([sQuery(id+"F0.wireOp",EDGE,"E19.MirrorCS")])],"isStart":false}),"instanceName":"1"});
            var Q10;
            Q10=makeQuery(id+"F3.opPattern","COPY",EDGE,{"derivedFrom":makeQuery(id+"F1.opExtrude","CAP_EDGE",EDGE,{"disambiguationData":[OSD([sQuery(id+"F0.wireOp",EDGE,"E18.MirrorCS")])],"isStart":false}),"instanceName":"1"});
            var Q11;
            Q11=makeQuery(id+"F3.opPattern","COPY",EDGE,{"derivedFrom":makeQuery(id+"F1.opExtrude","CAP_EDGE",EDGE,{"disambiguationData":[OSD([sQuery(id+"F0.wireOp",EDGE,"E9")])],"isStart":false}),"instanceName":"1"});
            var Q12;
            Q12=makeQuery(id+"F3.opPattern","COPY",EDGE,{"derivedFrom":makeQuery(id+"F1.opExtrude","CAP_EDGE",EDGE,{"disambiguationData":[OSD([sQuery(id+"F0.wireOp",EDGE,"E10")])],"isStart":false}),"instanceName":"1"});
            var Q13;
            Q13=makeQuery(id+"F3.opPattern","COPY",EDGE,{"derivedFrom":makeQuery(id+"F1.opExtrude","CAP_EDGE",EDGE,{"disambiguationData":[OSD([sQuery(id+"F0.wireOp",EDGE,"E11")])],"isStart":false}),"instanceName":"1"});
            var Q14;
            Q14=makeQuery(id+"F3.opPattern","COPY",EDGE,{"derivedFrom":makeQuery(id+"F1.opExtrude","CAP_EDGE",EDGE,{"disambiguationData":[OSD([sQuery(id+"F0.wireOp",EDGE,"E12")])],"isStart":false}),"instanceName":"1"});
            var Q15;
            Q15=makeQuery(id+"F1.opExtrude","CAP_EDGE",EDGE,{"disambiguationData":[OSD([sQuery(id+"F0.wireOp",EDGE,"E25.MirrorCS")])],"isStart":false});
            var Q16;
            Q16=makeQuery(id+"F1.opExtrude","CAP_EDGE",EDGE,{"disambiguationData":[OSD([sQuery(id+"F0.wireOp",EDGE,"E20.MirrorCS")])],"isStart":false});
            var Q17;
            Q17=makeQuery(id+"F1.opExtrude","CAP_EDGE",EDGE,{"disambiguationData":[OSD([sQuery(id+"F0.wireOp",EDGE,"E19.MirrorCS")])],"isStart":false});
            var Q18;
            Q18=makeQuery(id+"F1.opExtrude","CAP_EDGE",EDGE,{"disambiguationData":[OSD([sQuery(id+"F0.wireOp",EDGE,"E18.MirrorCS")])],"isStart":false});
            var Q19;
            Q19=makeQuery(id+"F1.opExtrude","CAP_EDGE",EDGE,{"disambiguationData":[OSD([sQuery(id+"F0.wireOp",EDGE,"E9")])],"isStart":false});
            var Q20;
            Q20=makeQuery(id+"F1.opExtrude","CAP_EDGE",EDGE,{"disambiguationData":[OSD([sQuery(id+"F0.wireOp",EDGE,"E10")])],"isStart":false});
            var Q21;
            Q21=makeQuery(id+"F1.opExtrude","CAP_EDGE",EDGE,{"disambiguationData":[OSD([sQuery(id+"F0.wireOp",EDGE,"E11")])],"isStart":false});
            var Q22;
            Q22=makeQuery(id+"F1.opExtrude","CAP_EDGE",EDGE,{"disambiguationData":[OSD([sQuery(id+"F0.wireOp",EDGE,"E12")])],"isStart":false});
            var Q23;
            Q23=makeQuery(id+"F3.opPattern","COPY",EDGE,{"derivedFrom":makeQuery(id+"F1.opExtrude","CAP_EDGE",EDGE,{"disambiguationData":[OSD([sQuery(id+"F0.wireOp",EDGE,"E25.MirrorCS")])],"isStart":false}),"instanceName":"5"});
            var Q24;
            Q24=makeQuery(id+"F3.opPattern","COPY",EDGE,{"derivedFrom":makeQuery(id+"F1.opExtrude","CAP_EDGE",EDGE,{"disambiguationData":[OSD([sQuery(id+"F0.wireOp",EDGE,"E20.MirrorCS")])],"isStart":false}),"instanceName":"5"});
            var Q25;
            Q25=makeQuery(id+"F3.opPattern","COPY",EDGE,{"derivedFrom":makeQuery(id+"F1.opExtrude","CAP_EDGE",EDGE,{"disambiguationData":[OSD([sQuery(id+"F0.wireOp",EDGE,"E19.MirrorCS")])],"isStart":false}),"instanceName":"5"});
            var Q26;
            Q26=makeQuery(id+"F3.opPattern","COPY",EDGE,{"derivedFrom":makeQuery(id+"F1.opExtrude","CAP_EDGE",EDGE,{"disambiguationData":[OSD([sQuery(id+"F0.wireOp",EDGE,"E18.MirrorCS")])],"isStart":false}),"instanceName":"5"});
            var Q27;
            Q27=makeQuery(id+"F3.opPattern","COPY",EDGE,{"derivedFrom":makeQuery(id+"F1.opExtrude","CAP_EDGE",EDGE,{"disambiguationData":[OSD([sQuery(id+"F0.wireOp",EDGE,"E9")])],"isStart":false}),"instanceName":"5"});
            var Q28;
            Q28=makeQuery(id+"F3.opPattern","COPY",EDGE,{"derivedFrom":makeQuery(id+"F1.opExtrude","CAP_EDGE",EDGE,{"disambiguationData":[OSD([sQuery(id+"F0.wireOp",EDGE,"E10")])],"isStart":false}),"instanceName":"5"});
            var Q29;
            Q29=makeQuery(id+"F3.opPattern","COPY",EDGE,{"derivedFrom":makeQuery(id+"F1.opExtrude","CAP_EDGE",EDGE,{"disambiguationData":[OSD([sQuery(id+"F0.wireOp",EDGE,"E11")])],"isStart":false}),"instanceName":"5"});
            var Q30;
            Q30=makeQuery(id+"F3.opPattern","COPY",EDGE,{"derivedFrom":makeQuery(id+"F1.opExtrude","CAP_EDGE",EDGE,{"disambiguationData":[OSD([sQuery(id+"F0.wireOp",EDGE,"E12")])],"isStart":false}),"instanceName":"5"});
            var Q31;
            Q31=makeQuery(id+"F3.opPattern","COPY",EDGE,{"derivedFrom":makeQuery(id+"F1.opExtrude","CAP_EDGE",EDGE,{"disambiguationData":[OSD([sQuery(id+"F0.wireOp",EDGE,"E25.MirrorCS")])],"isStart":false}),"instanceName":"4"});
            var Q32;
            Q32=makeQuery(id+"F3.opPattern","COPY",EDGE,{"derivedFrom":makeQuery(id+"F1.opExtrude","CAP_EDGE",EDGE,{"disambiguationData":[OSD([sQuery(id+"F0.wireOp",EDGE,"E20.MirrorCS")])],"isStart":false}),"instanceName":"4"});
            var Q33;
            Q33=makeQuery(id+"F3.opPattern","COPY",EDGE,{"derivedFrom":makeQuery(id+"F1.opExtrude","CAP_EDGE",EDGE,{"disambiguationData":[OSD([sQuery(id+"F0.wireOp",EDGE,"E19.MirrorCS")])],"isStart":false}),"instanceName":"4"});
            var Q34;
            Q34=makeQuery(id+"F3.opPattern","COPY",EDGE,{"derivedFrom":makeQuery(id+"F1.opExtrude","CAP_EDGE",EDGE,{"disambiguationData":[OSD([sQuery(id+"F0.wireOp",EDGE,"E18.MirrorCS")])],"isStart":false}),"instanceName":"4"});
            var Q35;
            Q35=makeQuery(id+"F3.opPattern","COPY",EDGE,{"derivedFrom":makeQuery(id+"F1.opExtrude","CAP_EDGE",EDGE,{"disambiguationData":[OSD([sQuery(id+"F0.wireOp",EDGE,"E9")])],"isStart":false}),"instanceName":"4"});
            var Q36;
            Q36=makeQuery(id+"F3.opPattern","COPY",EDGE,{"derivedFrom":makeQuery(id+"F1.opExtrude","CAP_EDGE",EDGE,{"disambiguationData":[OSD([sQuery(id+"F0.wireOp",EDGE,"E10")])],"isStart":false}),"instanceName":"4"});
            var Q37;
            Q37=makeQuery(id+"F3.opPattern","COPY",EDGE,{"derivedFrom":makeQuery(id+"F1.opExtrude","CAP_EDGE",EDGE,{"disambiguationData":[OSD([sQuery(id+"F0.wireOp",EDGE,"E11")])],"isStart":false}),"instanceName":"4"});
            var Q38;
            Q38=makeQuery(id+"F3.opPattern","COPY",EDGE,{"derivedFrom":makeQuery(id+"F1.opExtrude","CAP_EDGE",EDGE,{"disambiguationData":[OSD([sQuery(id+"F0.wireOp",EDGE,"E12")])],"isStart":false}),"instanceName":"4"});
            var Q39;
            Q39=makeQuery(id+"F3.opPattern","COPY",EDGE,{"derivedFrom":makeQuery(id+"F1.opExtrude","CAP_EDGE",EDGE,{"disambiguationData":[OSD([sQuery(id+"F0.wireOp",EDGE,"E18.MirrorCS")])],"isStart":false}),"instanceName":"3"});
            var Q40;
            Q40=makeQuery(id+"F3.opPattern","COPY",EDGE,{"derivedFrom":makeQuery(id+"F1.opExtrude","CAP_EDGE",EDGE,{"disambiguationData":[OSD([sQuery(id+"F0.wireOp",EDGE,"E19.MirrorCS")])],"isStart":false}),"instanceName":"3"});
            var Q41;
            Q41=makeQuery(id+"F3.opPattern","COPY",EDGE,{"derivedFrom":makeQuery(id+"F1.opExtrude","CAP_EDGE",EDGE,{"disambiguationData":[OSD([sQuery(id+"F0.wireOp",EDGE,"E20.MirrorCS")])],"isStart":false}),"instanceName":"3"});
            var Q42;
            Q42=makeQuery(id+"F3.opPattern","COPY",EDGE,{"derivedFrom":makeQuery(id+"F1.opExtrude","CAP_EDGE",EDGE,{"disambiguationData":[OSD([sQuery(id+"F0.wireOp",EDGE,"E25.MirrorCS")])],"isStart":false}),"instanceName":"3"});
            var Q43;
            Q43=makeQuery(id+"F3.opPattern","COPY",EDGE,{"derivedFrom":makeQuery(id+"F1.opExtrude","CAP_EDGE",EDGE,{"disambiguationData":[OSD([sQuery(id+"F0.wireOp",EDGE,"E9")])],"isStart":false}),"instanceName":"3"});
            var Q44;
            Q44=makeQuery(id+"F3.opPattern","COPY",EDGE,{"derivedFrom":makeQuery(id+"F1.opExtrude","CAP_EDGE",EDGE,{"disambiguationData":[OSD([sQuery(id+"F0.wireOp",EDGE,"E10")])],"isStart":false}),"instanceName":"3"});
            var Q45;
            Q45=makeQuery(id+"F3.opPattern","COPY",EDGE,{"derivedFrom":makeQuery(id+"F1.opExtrude","CAP_EDGE",EDGE,{"disambiguationData":[OSD([sQuery(id+"F0.wireOp",EDGE,"E11")])],"isStart":false}),"instanceName":"3"});
            var Q46;
            Q46=makeQuery(id+"F3.opPattern","COPY",EDGE,{"derivedFrom":makeQuery(id+"F1.opExtrude","CAP_EDGE",EDGE,{"disambiguationData":[OSD([sQuery(id+"F0.wireOp",EDGE,"E12")])],"isStart":false}),"instanceName":"3"});
            var Q47;
            Q47=makeQuery(id+"F3.opPattern","COPY",EDGE,{"derivedFrom":makeQuery(id+"F1.opExtrude","CAP_EDGE",EDGE,{"disambiguationData":[OSD([sQuery(id+"F0.wireOp",EDGE,"E25.MirrorCS")])],"isStart":false}),"instanceName":"1"});
            chamfer(context, id + "F7", {"entities" : qUnion([Q0, Q1, Q2, Q3, Q4, Q5, Q6, Q7, Q8, Q9, Q10, Q11, Q12, Q13, Q14, Q15, Q16, Q17, Q18, Q19, Q20, Q21, Q22, Q23, Q24, Q25, Q26, Q27, Q28, Q29, Q30, Q31, Q32, Q33, Q34, Q35, Q36, Q37, Q38, Q39, Q40, Q41, Q42, Q43, Q44, Q45, Q46, Q47]), "width" : .8 * mm, "tangentPropagation" : true});
        }
        {
            var Q0;
            Q0=makeQuery(id+"F3.opPattern","COPY",EDGE,{"derivedFrom":makeQuery(id+"F1.opExtrude","CAP_EDGE",EDGE,{"disambiguationData":[OSD([sQuery(id+"F0.wireOp",EDGE,"E30.MirrorCS")])],"isStart":false}),"instanceName":"2"});
            var Q1;
            Q1=makeQuery(id+"F3.opPattern","COPY",EDGE,{"derivedFrom":makeQuery(id+"F1.opExtrude","CAP_EDGE",EDGE,{"disambiguationData":[OSD([sQuery(id+"F0.wireOp",EDGE,"E13")])],"isStart":false}),"instanceName":"2"});
            var Q2;
            Q2=makeQuery(id+"F3.opPattern","COPY",EDGE,{"derivedFrom":makeQuery(id+"F1.opExtrude","CAP_EDGE",EDGE,{"disambiguationData":[OSD([sQuery(id+"F0.wireOp",EDGE,"E30.MirrorCS")])],"isStart":false}),"instanceName":"1"});
            var Q3;
            Q3=makeQuery(id+"F3.opPattern","COPY",EDGE,{"derivedFrom":makeQuery(id+"F1.opExtrude","CAP_EDGE",EDGE,{"disambiguationData":[OSD([sQuery(id+"F0.wireOp",EDGE,"E13")])],"isStart":false}),"instanceName":"1"});
            var Q4;
            Q4=makeQuery(id+"F1.opExtrude","CAP_EDGE",EDGE,{"disambiguationData":[OSD([sQuery(id+"F0.wireOp",EDGE,"E30.MirrorCS")])],"isStart":false});
            var Q5;
            Q5=makeQuery(id+"F1.opExtrude","CAP_EDGE",EDGE,{"disambiguationData":[OSD([sQuery(id+"F0.wireOp",EDGE,"E13")])],"isStart":false});
            var Q6;
            Q6=makeQuery(id+"F3.opPattern","COPY",EDGE,{"derivedFrom":makeQuery(id+"F1.opExtrude","CAP_EDGE",EDGE,{"disambiguationData":[OSD([sQuery(id+"F0.wireOp",EDGE,"E30.MirrorCS")])],"isStart":false}),"instanceName":"5"});
            var Q7;
            Q7=makeQuery(id+"F3.opPattern","COPY",EDGE,{"derivedFrom":makeQuery(id+"F1.opExtrude","CAP_EDGE",EDGE,{"disambiguationData":[OSD([sQuery(id+"F0.wireOp",EDGE,"E13")])],"isStart":false}),"instanceName":"5"});
            var Q8;
            Q8=makeQuery(id+"F3.opPattern","COPY",EDGE,{"derivedFrom":makeQuery(id+"F1.opExtrude","CAP_EDGE",EDGE,{"disambiguationData":[OSD([sQuery(id+"F0.wireOp",EDGE,"E30.MirrorCS")])],"isStart":false}),"instanceName":"4"});
            var Q9;
            Q9=makeQuery(id+"F3.opPattern","COPY",EDGE,{"derivedFrom":makeQuery(id+"F1.opExtrude","CAP_EDGE",EDGE,{"disambiguationData":[OSD([sQuery(id+"F0.wireOp",EDGE,"E13")])],"isStart":false}),"instanceName":"4"});
            var Q10;
            Q10=makeQuery(id+"F3.opPattern","COPY",EDGE,{"derivedFrom":makeQuery(id+"F1.opExtrude","CAP_EDGE",EDGE,{"disambiguationData":[OSD([sQuery(id+"F0.wireOp",EDGE,"E30.MirrorCS")])],"isStart":false}),"instanceName":"3"});
            var Q11;
            Q11=makeQuery(id+"F3.opPattern","COPY",EDGE,{"derivedFrom":makeQuery(id+"F1.opExtrude","CAP_EDGE",EDGE,{"disambiguationData":[OSD([sQuery(id+"F0.wireOp",EDGE,"E13")])],"isStart":false}),"instanceName":"3"});
            chamfer(context, id + "F8", {"entities" : qUnion([Q0, Q1, Q2, Q3, Q4, Q5, Q6, Q7, Q8, Q9, Q10, Q11]), "width" : 1.26 * mm, "tangentPropagation" : true});
        }
        {
            var Q0;
            Q0=makeQuery(id+"F3.opPattern","COPY",EDGE,{"derivedFrom":makeQuery(id+"F1.opExtrude","CAP_EDGE",EDGE,{"disambiguationData":[OSD([sQuery(id+"F0.wireOp",EDGE,"E32")])],"isStart":false}),"instanceName":"2"});
            var Q1;
            Q1=makeQuery(id+"F3.opPattern","COPY",EDGE,{"derivedFrom":makeQuery(id+"F1.opExtrude","CAP_EDGE",EDGE,{"disambiguationData":[OSD([sQuery(id+"F0.wireOp",EDGE,"E33.MirrorCS")])],"isStart":false}),"instanceName":"1"});
            var Q2;
            Q2=makeQuery(id+"F3.opPattern","COPY",EDGE,{"derivedFrom":makeQuery(id+"F1.opExtrude","CAP_EDGE",EDGE,{"disambiguationData":[OSD([sQuery(id+"F0.wireOp",EDGE,"E32")])],"isStart":false}),"instanceName":"1"});
            var Q3;
            Q3=makeQuery(id+"F1.opExtrude","CAP_EDGE",EDGE,{"disambiguationData":[OSD([sQuery(id+"F0.wireOp",EDGE,"E33.MirrorCS")])],"isStart":false});
            var Q4;
            Q4=makeQuery(id+"F1.opExtrude","CAP_EDGE",EDGE,{"disambiguationData":[OSD([sQuery(id+"F0.wireOp",EDGE,"E32")])],"isStart":false});
            var Q5;
            Q5=makeQuery(id+"F3.opPattern","COPY",EDGE,{"derivedFrom":makeQuery(id+"F1.opExtrude","CAP_EDGE",EDGE,{"disambiguationData":[OSD([sQuery(id+"F0.wireOp",EDGE,"E33.MirrorCS")])],"isStart":false}),"instanceName":"5"});
            var Q6;
            Q6=makeQuery(id+"F3.opPattern","COPY",EDGE,{"derivedFrom":makeQuery(id+"F1.opExtrude","CAP_EDGE",EDGE,{"disambiguationData":[OSD([sQuery(id+"F0.wireOp",EDGE,"E32")])],"isStart":false}),"instanceName":"5"});
            var Q7;
            Q7=makeQuery(id+"F3.opPattern","COPY",EDGE,{"derivedFrom":makeQuery(id+"F1.opExtrude","CAP_EDGE",EDGE,{"disambiguationData":[OSD([sQuery(id+"F0.wireOp",EDGE,"E33.MirrorCS")])],"isStart":false}),"instanceName":"4"});
            var Q8;
            Q8=makeQuery(id+"F3.opPattern","COPY",EDGE,{"derivedFrom":makeQuery(id+"F1.opExtrude","CAP_EDGE",EDGE,{"disambiguationData":[OSD([sQuery(id+"F0.wireOp",EDGE,"E32")])],"isStart":false}),"instanceName":"4"});
            var Q9;
            Q9=makeQuery(id+"F3.opPattern","COPY",EDGE,{"derivedFrom":makeQuery(id+"F1.opExtrude","CAP_EDGE",EDGE,{"disambiguationData":[OSD([sQuery(id+"F0.wireOp",EDGE,"E33.MirrorCS")])],"isStart":false}),"instanceName":"3"});
            var Q10;
            Q10=makeQuery(id+"F3.opPattern","COPY",EDGE,{"derivedFrom":makeQuery(id+"F1.opExtrude","CAP_EDGE",EDGE,{"disambiguationData":[OSD([sQuery(id+"F0.wireOp",EDGE,"E32")])],"isStart":false}),"instanceName":"3"});
            var Q11;
            Q11=makeQuery(id+"F3.opPattern","COPY",EDGE,{"derivedFrom":makeQuery(id+"F1.opExtrude","CAP_EDGE",EDGE,{"disambiguationData":[OSD([sQuery(id+"F0.wireOp",EDGE,"E33.MirrorCS")])],"isStart":false}),"instanceName":"2"});
            chamfer(context, id + "F9", {"entities" : qUnion([Q0, Q1, Q2, Q3, Q4, Q5, Q6, Q7, Q8, Q9, Q10, Q11]), "width" : .5 * mm, "tangentPropagation" : true});
        }
        {
            var Q0;
            Q0=qCreatedBy(makeId("Right.planeOp"),FACE);
            var sketch = newSketch(context, id + "F10", { "sketchPlane" : qUnion([Q0])});
            skLineSegment(sketch, "E36.0", {"start": v(25, -0.75) * mm, "end": v(22, -0.75) * mm});
            skLineSegment(sketch, "E37.0", {"start": v(25, 0.01) * mm, "end": v(25, -0.75) * mm});
            skCircle(sketch, "E38", {"center": v(22, -0.75) * mm, "radius": 0.57 * mm});
            skSolve(sketch);
        }
        {
            var Q0;
            Q0 = qSketchRegion(id + "F10", true);
            extrude(context, id + "F11", {"entities" : qUnion([Q0]), "operationType" : NewBodyOperationType.REMOVE, "endBound" : BoundingType.SYMMETRIC, "oppositeDirection" : true, "depth" : 25 * mm});
        }
        {
            var Q0;
            {var subQ0=sQuery(id+"F0.wireOp",EDGE,"E15.MirrorCS");var subQ2=sQuery(id+"F0.wireOp",EDGE,"E14");var subQ4=sQuery(id+"F0.wireOp",EDGE,"E13");var subQ6=sQuery(id+"F0.wireOp",EDGE,"E12");var subQ8=sQuery(id+"F0.wireOp",EDGE,"E11");var subQ10=sQuery(id+"F0.wireOp",EDGE,"E10");var subQ12=sQuery(id+"F0.wireOp",EDGE,"E9");var subQ14=sQuery(id+"F0.wireOp",EDGE,"E8");var subQ16=sQuery(id+"F0.wireOp",EDGE,"E7");var subQ18=sQuery(id+"F0.wireOp",EDGE,"E6");var subQ20=sQuery(id+"F0.wireOp",EDGE,"E5");var subQ22=sQuery(id+"F0.wireOp",EDGE,"E4");var subQ23=makeQuery(id+"F1.opExtrude","SWEPT_FACE",FACE,{"disambiguationData":[OSD([subQ22])]});var subQ24=sQuery(id+"F0.wireOp",EDGE,"E3");var subQ26=sQuery(id+"F0.wireOp",EDGE,"E2");var subQ28=sQuery(id+"F0.wireOp",EDGE,"E33.MirrorCS");var subQ30=sQuery(id+"F0.wireOp",EDGE,"E32");var subQ32=sQuery(id+"F0.wireOp",EDGE,"E31.MirrorCS");var subQ34=sQuery(id+"F0.wireOp",EDGE,"E30.MirrorCS");var subQ36=sQuery(id+"F0.wireOp",EDGE,"E25.MirrorCS");var subQ38=sQuery(id+"F0.wireOp",EDGE,"E24.MirrorCS");var subQ40=sQuery(id+"F0.wireOp",EDGE,"E23.MirrorCS");var subQ42=sQuery(id+"F0.wireOp",EDGE,"E22.MirrorCS");var subQ44=sQuery(id+"F0.wireOp",EDGE,"E21.MirrorCS");var subQ46=sQuery(id+"F0.wireOp",EDGE,"E20.MirrorCS");var subQ48=sQuery(id+"F0.wireOp",EDGE,"E19.MirrorCS");var subQ50=sQuery(id+"F0.wireOp",EDGE,"E18.MirrorCS");var subQ52=sQuery(id+"F0.wireOp",EDGE,"E17.MirrorCS");var subQ54=sQuery(id+"F0.wireOp",EDGE,"E16.MirrorCS");var subQ56=makeQuery(id+"F1.opExtrude","CAP_FACE",FACE,{"disambiguationData":[OSD([subQ26,subQ24,subQ22,subQ20,subQ18,subQ16,subQ14,subQ12,subQ10,subQ8,subQ6,subQ4,subQ2,subQ0,subQ54,subQ52,subQ50,subQ48,subQ46,subQ44,subQ42,subQ40,subQ38,subQ36,sQuery(id+"F0.wireOp",EDGE,"E29"),subQ34,subQ32,subQ30,subQ28,sQuery(id+"F0.wireOp",EDGE,"E34.MirrorCS")])],"isStart":true});Q0=makeQuery(id+"F11.boolean.opBoolean","SPLIT",FACE,{"disambiguationData":[TD([subQ23])],"derivedFrom":makeQuery(id+"F3.boolean.opBoolean","MERGE",FACE,{"derivedFrom":[subQ56,makeQuery(id+"F3.opPattern","COPY",FACE,{"derivedFrom":subQ56,"instanceName":"1"}),makeQuery(id+"F3.opPattern","COPY",FACE,{"derivedFrom":subQ56,"instanceName":"2"}),makeQuery(id+"F3.opPattern","COPY",FACE,{"derivedFrom":subQ56,"instanceName":"3"}),makeQuery(id+"F3.opPattern","COPY",FACE,{"derivedFrom":subQ56,"instanceName":"4"}),makeQuery(id+"F3.opPattern","COPY",FACE,{"derivedFrom":subQ56,"instanceName":"5"})]})});}
            var Q1;
            {var subQ0=sQuery(id+"F0.wireOp",EDGE,"E22.MirrorCS");var subQ1=sQuery(id+"F0.wireOp",EDGE,"E2");var subQ2=sQuery(id+"F0.wireOp",EDGE,"E3");var subQ3=sQuery(id+"F0.wireOp",EDGE,"E15.MirrorCS");var subQ4=makeQuery(id+"F1.opExtrude","CAP_FACE",FACE,{"disambiguationData":[OSD([subQ1,subQ2,sQuery(id+"F0.wireOp",EDGE,"E4"),sQuery(id+"F0.wireOp",EDGE,"E5"),sQuery(id+"F0.wireOp",EDGE,"E6"),sQuery(id+"F0.wireOp",EDGE,"E7"),sQuery(id+"F0.wireOp",EDGE,"E8"),sQuery(id+"F0.wireOp",EDGE,"E9"),sQuery(id+"F0.wireOp",EDGE,"E10"),sQuery(id+"F0.wireOp",EDGE,"E11"),sQuery(id+"F0.wireOp",EDGE,"E12"),sQuery(id+"F0.wireOp",EDGE,"E13"),sQuery(id+"F0.wireOp",EDGE,"E14"),subQ3,sQuery(id+"F0.wireOp",EDGE,"E16.MirrorCS"),sQuery(id+"F0.wireOp",EDGE,"E17.MirrorCS"),sQuery(id+"F0.wireOp",EDGE,"E18.MirrorCS"),sQuery(id+"F0.wireOp",EDGE,"E19.MirrorCS"),sQuery(id+"F0.wireOp",EDGE,"E20.MirrorCS"),sQuery(id+"F0.wireOp",EDGE,"E21.MirrorCS"),subQ0,sQuery(id+"F0.wireOp",EDGE,"E23.MirrorCS"),sQuery(id+"F0.wireOp",EDGE,"E24.MirrorCS"),sQuery(id+"F0.wireOp",EDGE,"E25.MirrorCS"),sQuery(id+"F0.wireOp",EDGE,"E29"),sQuery(id+"F0.wireOp",EDGE,"E30.MirrorCS"),sQuery(id+"F0.wireOp",EDGE,"E31.MirrorCS"),sQuery(id+"F0.wireOp",EDGE,"E32"),sQuery(id+"F0.wireOp",EDGE,"E33.MirrorCS"),sQuery(id+"F0.wireOp",EDGE,"E34.MirrorCS")])],"isStart":true});Q1=makeQuery(id+"F11.boolean.opBoolean","SPLIT",FACE,{"disambiguationData":[TD([makeQuery(id+"F1.opExtrude","SWEPT_FACE",FACE,{"disambiguationData":[OSD([subQ1])]})])],"derivedFrom":makeQuery(id+"F3.boolean.opBoolean","MERGE",FACE,{"derivedFrom":[subQ4,makeQuery(id+"F3.opPattern","COPY",FACE,{"derivedFrom":subQ4,"instanceName":"1"}),makeQuery(id+"F3.opPattern","COPY",FACE,{"derivedFrom":subQ4,"instanceName":"2"}),makeQuery(id+"F3.opPattern","COPY",FACE,{"derivedFrom":subQ4,"instanceName":"3"}),makeQuery(id+"F3.opPattern","COPY",FACE,{"derivedFrom":subQ4,"instanceName":"4"}),makeQuery(id+"F3.opPattern","COPY",FACE,{"derivedFrom":subQ4,"instanceName":"5"})]})});}
            chamfer(context, id + "F12", {"entities" : qUnion([Q0, Q1]), "width" : .14 * mm, "tangentPropagation" : true});
        }
    });
